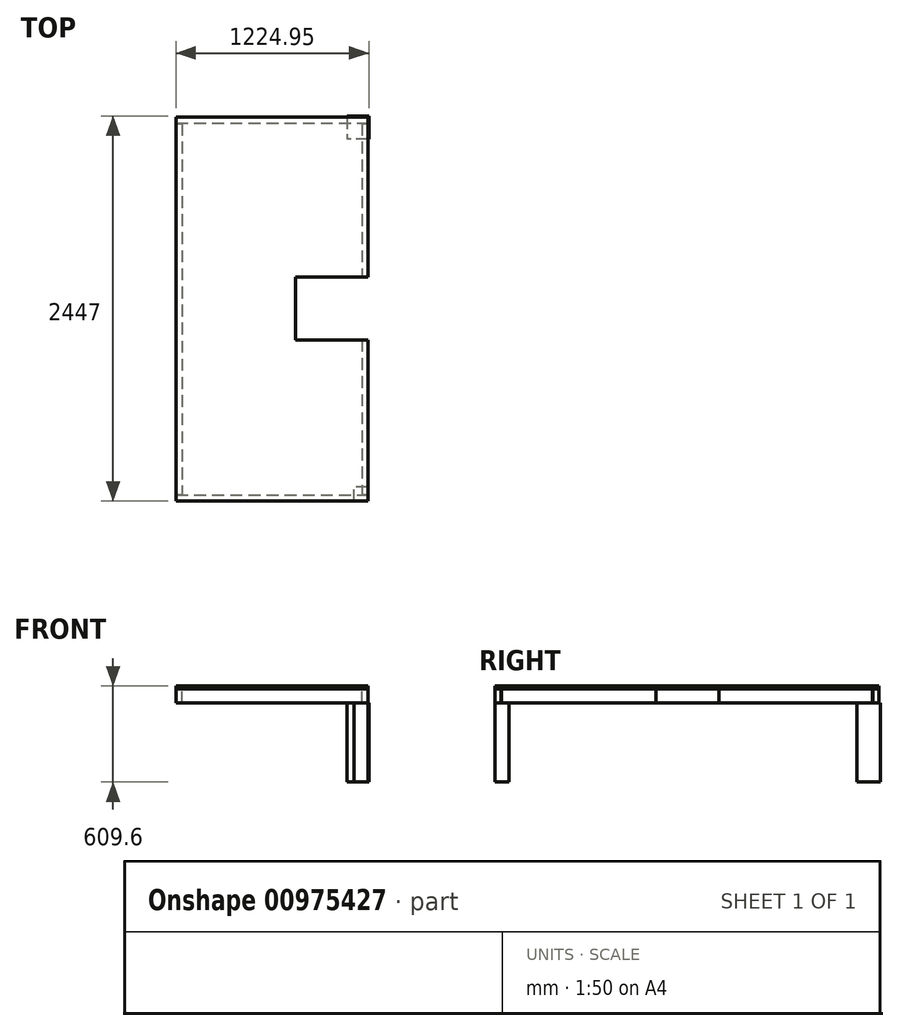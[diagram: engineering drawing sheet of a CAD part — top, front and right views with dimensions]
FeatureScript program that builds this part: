
annotation { "Feature Type Name" : "Feature", "Feature Type Description" : "" }
export const myFeature = defineFeature(function(context is Context, id is Id, definition is map)
    precondition{}
    {
        {
            var Q0;
            Q0=qCreatedBy(makeId("Top.planeOp"),FACE);
            var sketch = newSketch(context, id + "F0", { "sketchPlane" : qUnion([Q0])});
            skLineSegment(sketch, "E0.bottom", {"start": v(-609.6, 1219.2) * mm, "end": v(609.6, 1219.2) * mm, "construction": true});
            skLineSegment(sketch, "E0.top", {"start": v(-609.6, -1219.2) * mm, "end": v(609.6, -1219.2) * mm, "construction": true});
            skLineSegment(sketch, "E0.left", {"start": v(-609.6, 1219.2) * mm, "end": v(-609.6, -1219.2) * mm, "construction": true});
            skLineSegment(sketch, "E0.right", {"start": v(609.6, 1219.2) * mm, "end": v(609.6, -1219.2) * mm, "construction": true});
            skSolve(sketch);
        }
        {
            var Q0;
            Q0=qCreatedBy(makeId("Top.planeOp"),FACE);
            var sketch = newSketch(context, id + "F1", { "sketchPlane" : qUnion([Q0])});
            skLineSegment(sketch, "E1.bottom", {"start": v(609.6, 1219.2) * mm, "end": v(-609.6, 1219.2) * mm});
            skLineSegment(sketch, "E1.top", {"start": v(609.6, -1219.2) * mm, "end": v(-609.6, -1219.2) * mm});
            skLineSegment(sketch, "E1.left", {"start": v(609.6, 1219.2) * mm, "end": v(609.6, -1219.2) * mm});
            skLineSegment(sketch, "E1.right", {"start": v(-609.6, 1219.2) * mm, "end": v(-609.6, -1219.2) * mm});
            skSolve(sketch);
        }
        {
            var Q0;
            Q0 = qSketchRegion(id + "F1", true);
            extrude(context, id + "F2", {"entities" : qUnion([Q0]), "depth" : 19.05 * mm, "offsetDistance" : 25.4 * mm});
        }
        {
            var Q0;
            Q0=qCreatedBy(makeId("Top.planeOp"),FACE);
            var sketch = newSketch(context, id + "F3", { "sketchPlane" : qUnion([Q0])});
            skLineSegment(sketch, "E2.bottom", {"start": v(-609.6, 1219.2) * mm, "end": v(609.6, 1219.2) * mm});
            skLineSegment(sketch, "E2.top", {"start": v(-609.6, 1181.1) * mm, "end": v(609.6, 1181.1) * mm});
            skLineSegment(sketch, "E2.left", {"start": v(-609.6, 1219.2) * mm, "end": v(-609.6, 1181.1) * mm});
            skLineSegment(sketch, "E2.right", {"start": v(609.6, 1219.2) * mm, "end": v(609.6, 1181.1) * mm});
            skLineSegment(sketch, "E3.bottom", {"start": v(-609.6, -1219.2) * mm, "end": v(609.6, -1219.2) * mm});
            skLineSegment(sketch, "E3.top", {"start": v(-609.6, -1181.1) * mm, "end": v(609.6, -1181.1) * mm});
            skLineSegment(sketch, "E3.left", {"start": v(-609.6, -1219.2) * mm, "end": v(-609.6, -1181.1) * mm});
            skLineSegment(sketch, "E3.right", {"start": v(609.6, -1219.2) * mm, "end": v(609.6, -1181.1) * mm});
            skSolve(sketch);
        }
        {
            var Q0;
            Q0 = qSketchRegion(id + "F3", true);
            extrude(context, id + "F4", {"entities" : qUnion([Q0]), "oppositeDirection" : true, "depth" : 88.9 * mm, "offsetDistance" : 25.4 * mm});
        }
        {
            var Q0;
            Q0=qCreatedBy(makeId("Top.planeOp"),FACE);
            var sketch = newSketch(context, id + "F5", { "sketchPlane" : qUnion([Q0])});
            skLineSegment(sketch, "E4.bottom", {"start": v(-609.6, 1178.56) * mm, "end": v(-571.5, 1178.56) * mm});
            skLineSegment(sketch, "E4.top", {"start": v(-609.6, -1178.56) * mm, "end": v(-571.5, -1178.56) * mm});
            skLineSegment(sketch, "E4.left", {"start": v(-609.6, 1178.56) * mm, "end": v(-609.6, -1178.56) * mm});
            skLineSegment(sketch, "E4.right", {"start": v(-571.5, 1178.56) * mm, "end": v(-571.5, -1178.56) * mm});
            skLineSegment(sketch, "E5.bottom", {"start": v(571.5, 1178.56) * mm, "end": v(609.6, 1178.56) * mm});
            skLineSegment(sketch, "E5.top", {"start": v(571.5, -1178.56) * mm, "end": v(609.6, -1178.56) * mm});
            skLineSegment(sketch, "E5.left", {"start": v(571.5, 1178.56) * mm, "end": v(571.5, -1178.56) * mm});
            skLineSegment(sketch, "E5.right", {"start": v(609.6, 1178.56) * mm, "end": v(609.6, -1178.56) * mm});
            skSolve(sketch);
        }
        {
            var Q0;
            Q0 = qSketchRegion(id + "F5", true);
            extrude(context, id + "F6", {"entities" : qUnion([Q0]), "oppositeDirection" : true, "depth" : 88.9 * mm, "offsetDistance" : 25.4 * mm});
        }
        {
            var Q0;
            Q0=makeQuery(id+"F2.opExtrude","CAP_FACE",FACE,{"disambiguationData":[OSD([sQuery(id+"F1.wireOp",EDGE,"E1.bottom"),sQuery(id+"F1.wireOp",EDGE,"E1.top"),sQuery(id+"F1.wireOp",EDGE,"E1.left"),sQuery(id+"F1.wireOp",EDGE,"E1.right")])],"isStart":false});
            var sketch = newSketch(context, id + "F7", { "sketchPlane" : qUnion([Q0])});
            skLineSegment(sketch, "E6.bottom", {"start": v(609.6, -195.6) * mm, "end": v(148.75, -195.6) * mm});
            skLineSegment(sketch, "E6.top", {"start": v(609.6, 204.97) * mm, "end": v(148.75, 204.97) * mm});
            skLineSegment(sketch, "E6.left", {"start": v(609.6, -195.6) * mm, "end": v(609.6, 204.97) * mm});
            skLineSegment(sketch, "E6.right", {"start": v(148.75, -195.6) * mm, "end": v(148.75, 204.97) * mm});
            skSolve(sketch);
        }
        {
            var Q0;
            Q0 = qSketchRegion(id + "F7", true);
            extrude(context, id + "F8", {"entities" : qUnion([Q0]), "operationType" : NewBodyOperationType.REMOVE, "endBound" : BoundingType.THROUGH_ALL, "oppositeDirection" : true, "depth" : 25.4 * mm, "offsetDistance" : 25.4 * mm});
        }
        {
            var Q0;
            Q0=makeQuery(id+"F2.opExtrude","CAP_FACE",FACE,{"disambiguationData":[OSD([sQuery(id+"F1.wireOp",EDGE,"E1.bottom"),sQuery(id+"F1.wireOp",EDGE,"E1.top"),sQuery(id+"F1.wireOp",EDGE,"E1.left"),sQuery(id+"F1.wireOp",EDGE,"E1.right")])],"isStart":false});
            cPlane(context, id + "F9", {"entities" : qUnion([Q0]), "cplaneType" : CPlaneType.OFFSET, "offset" : 609.6 * mm, "oppositeDirection" : true, "width" : 152.4 * mm, "height" : 152.4 * mm});
        }
        {
            var Q0;
            Q0=qCreatedBy(id+"F9.planeOp",FACE);
            var sketch = newSketch(context, id + "F10", { "sketchPlane" : qUnion([Q0])});
            skLineSegment(sketch, "E7.bottom", {"start": v(609.6, -1219.2) * mm, "end": v(520.7, -1219.2) * mm});
            skLineSegment(sketch, "E7.top", {"start": v(609.6, -1130.3) * mm, "end": v(520.7, -1130.3) * mm});
            skLineSegment(sketch, "E7.left", {"start": v(609.6, -1219.2) * mm, "end": v(609.6, -1130.3) * mm});
            skLineSegment(sketch, "E7.right", {"start": v(520.7, -1219.2) * mm, "end": v(520.7, -1130.3) * mm});
            skLineSegment(sketch, "E8.bottom", {"start": v(615.35, 1227.8) * mm, "end": v(476.07, 1227.8) * mm});
            skLineSegment(sketch, "E8.top", {"start": v(615.35, 1080.16) * mm, "end": v(476.07, 1080.16) * mm});
            skLineSegment(sketch, "E8.left", {"start": v(615.35, 1227.8) * mm, "end": v(615.35, 1080.16) * mm});
            skLineSegment(sketch, "E8.right", {"start": v(476.07, 1227.8) * mm, "end": v(476.07, 1080.16) * mm});
            skSolve(sketch);
        }
        {
            var Q0;
            Q0 = qSketchRegion(id + "F10", true);
            var Q1;
            Q1=makeQuery(id+"F4.opExtrude","CAP_FACE",FACE,{"disambiguationData":[OSD([sQuery(id+"F3.wireOp",EDGE,"E3.bottom"),sQuery(id+"F3.wireOp",EDGE,"E3.top"),sQuery(id+"F3.wireOp",EDGE,"E3.left"),sQuery(id+"F3.wireOp",EDGE,"E3.right")])],"isStart":false});
            extrude(context, id + "F11", {"entities" : qUnion([Q0]), "endBound" : BoundingType.UP_TO_SURFACE, "depth" : 25.4 * mm, "endBoundEntityFace" : qUnion([Q1]), "offsetDistance" : 25.4 * mm});
        }
    });
